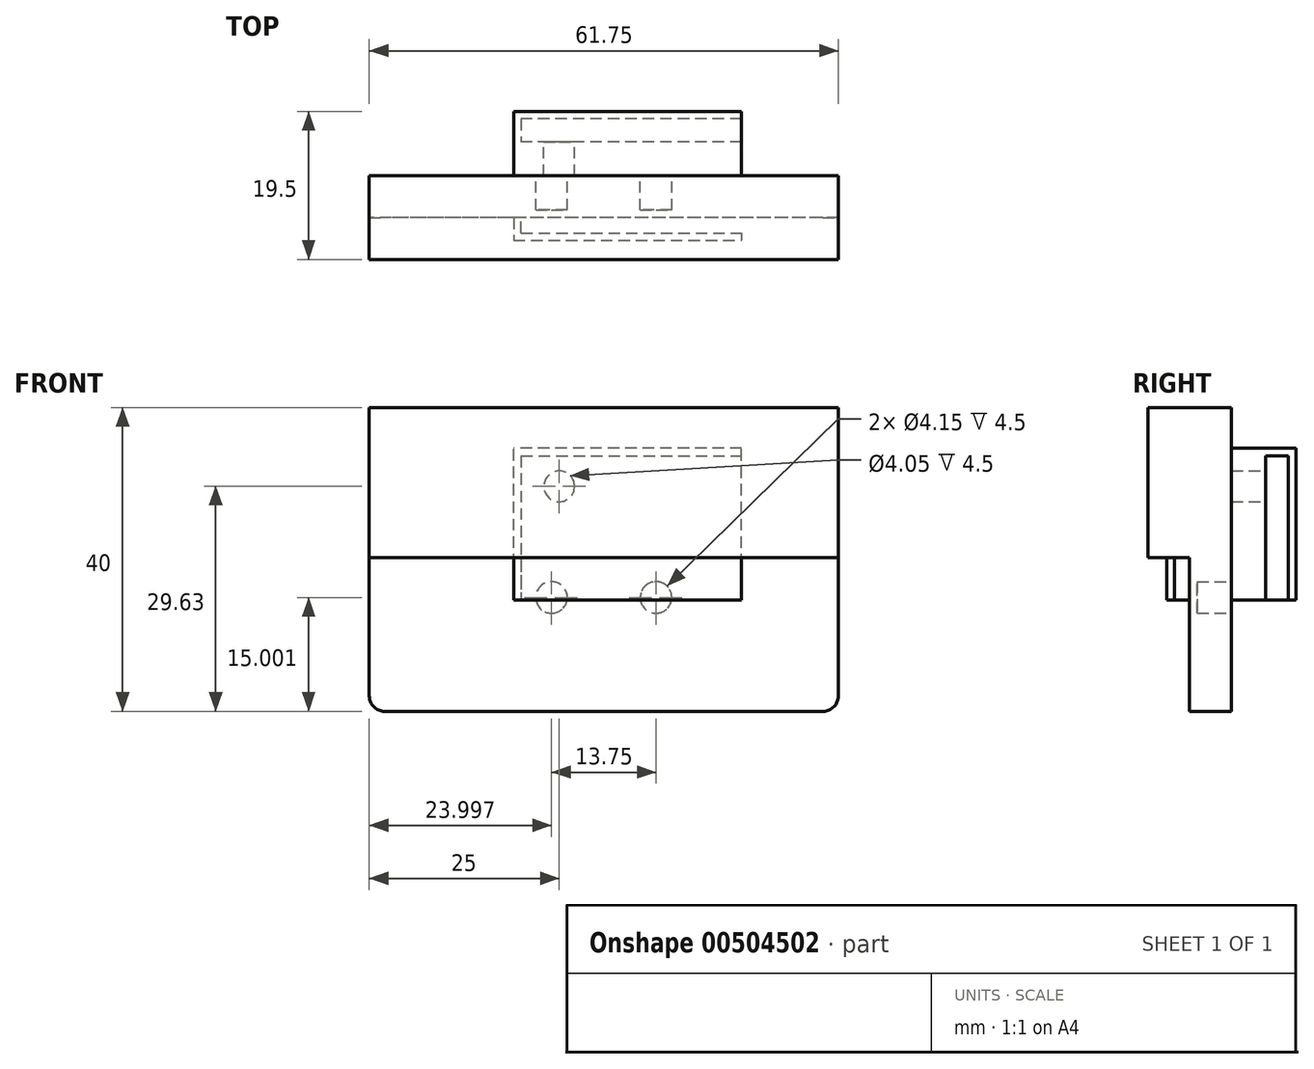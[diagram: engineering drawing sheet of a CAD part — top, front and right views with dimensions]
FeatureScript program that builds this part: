
annotation { "Feature Type Name" : "Feature", "Feature Type Description" : "" }
export const myFeature = defineFeature(function(context is Context, id is Id, definition is map)
    precondition{}
    {
        {
            var Q0;
            Q0=qCreatedBy(makeId("Front.planeOp"),FACE);
            var sketch = newSketch(context, id + "F0", { "sketchPlane" : qUnion([Q0])});
            skLineSegment(sketch, "E0.bottom", {"start": v(15, -10) * mm, "end": v(-15, -10) * mm});
            skLineSegment(sketch, "E0.top", {"start": v(15, 10) * mm, "end": v(-15, 10) * mm});
            skLineSegment(sketch, "E0.left", {"start": v(15, -10) * mm, "end": v(15, 10) * mm});
            skLineSegment(sketch, "E0.right", {"start": v(-15, -10) * mm, "end": v(-15, 10) * mm});
            skPoint(sketch, "E0.middle", {"position": v(0, 0) * mm});
            skPoint(sketch, "E1", {"position": v(-14, 9) * mm});
            skLineSegment(sketch, "E2", {"start": v(-14, 9) * mm, "end": v(15, 9) * mm});
            skLineSegment(sketch, "E3", {"start": v(-14, 9) * mm, "end": v(-14, -10) * mm});
            skCircle(sketch, "E4", {"center": v(-9, 5) * mm, "radius": 2.02 * mm});
            skSolve(sketch);
        }
        {
            var Q0;
            {var subQ1=sQuery(id+"F0.wireOp",EDGE,"E2");Q0=makeQuery(id+"F0.imprint","IMPRINT",FACE,{"disambiguationData":[TD([[makeQuery(id+"F0.imprint","IMPRINT",EDGE,{"derivedFrom":subQ1}),-1.0]])]});}
            var Q1;
            {var subQ2=sQuery(id+"F0.wireOp",EDGE,"E0.top");Q1=makeQuery(id+"F0.imprint","IMPRINT",FACE,{"disambiguationData":[TD([[makeQuery(id+"F0.imprint","IMPRINT",EDGE,{"derivedFrom":subQ2}),1.0]])]});}
            var Q2;
            Q2=makeQuery(id+"F0.imprint","IMPRINT",FACE,{"disambiguationData":[TD([[makeQuery(id+"F0.imprint","IMPRINT",EDGE,{"derivedFrom":sQuery(id+"F0.wireOp",EDGE,"E4")}),1.0]])]});
            extrude(context, id + "F1", {"entities" : qUnion([Q0, Q1, Q2]), "depth" : 8.5 * mm});
        }
        {
            var Q0;
            {var subQ1=sQuery(id+"F0.wireOp",EDGE,"E2");Q0=makeQuery(id+"F0.imprint","IMPRINT",FACE,{"disambiguationData":[TD([[makeQuery(id+"F0.imprint","IMPRINT",EDGE,{"derivedFrom":subQ1}),-1.0]])]});}
            var Q1;
            Q1=makeQuery(id+"F0.imprint","IMPRINT",FACE,{"disambiguationData":[TD([[makeQuery(id+"F0.imprint","IMPRINT",EDGE,{"derivedFrom":sQuery(id+"F0.wireOp",EDGE,"E4")}),1.0]])]});
            extrude(context, id + "F2", {"entities" : qUnion([Q0, Q1]), "operationType" : NewBodyOperationType.REMOVE, "depth" : 7.5 * mm});
        }
        {
            var Q0;
            {var subQ1=sQuery(id+"F0.wireOp",EDGE,"E2");Q0=makeQuery(id+"F0.imprint","IMPRINT",FACE,{"disambiguationData":[TD([[makeQuery(id+"F0.imprint","IMPRINT",EDGE,{"derivedFrom":subQ1}),-1.0]])]});}
            extrude(context, id + "F3", {"entities" : qUnion([Q0]), "operationType" : NewBodyOperationType.ADD, "depth" : 4.5 * mm});
        }
        {
            var Q0;
            {var subQ1=sQuery(id+"F0.wireOp",EDGE,"E2");Q0=makeQuery(id+"F0.imprint","IMPRINT",FACE,{"disambiguationData":[TD([[makeQuery(id+"F0.imprint","IMPRINT",EDGE,{"derivedFrom":subQ1}),-1.0]])]});}
            var Q1;
            Q1=makeQuery(id+"F0.imprint","IMPRINT",FACE,{"disambiguationData":[TD([[makeQuery(id+"F0.imprint","IMPRINT",EDGE,{"derivedFrom":sQuery(id+"F0.wireOp",EDGE,"E4")}),1.0]])]});
            var Q2;
            {var subQ2=sQuery(id+"F0.wireOp",EDGE,"E0.top");Q2=makeQuery(id+"F0.imprint","IMPRINT",FACE,{"disambiguationData":[TD([[makeQuery(id+"F0.imprint","IMPRINT",EDGE,{"derivedFrom":subQ2}),1.0]])]});}
            extrude(context, id + "F4", {"entities" : qUnion([Q0, Q1, Q2]), "oppositeDirection" : true, "depth" : 8.5 * mm});
        }
        {
            var Q0;
            {var subQ1=sQuery(id+"F0.wireOp",EDGE,"E2");Q0=makeQuery(id+"F0.imprint","IMPRINT",FACE,{"disambiguationData":[TD([[makeQuery(id+"F0.imprint","IMPRINT",EDGE,{"derivedFrom":subQ1}),-1.0]])]});}
            var Q1;
            Q1=makeQuery(id+"F0.imprint","IMPRINT",FACE,{"disambiguationData":[TD([[makeQuery(id+"F0.imprint","IMPRINT",EDGE,{"derivedFrom":sQuery(id+"F0.wireOp",EDGE,"E4")}),1.0]])]});
            extrude(context, id + "F5", {"entities" : qUnion([Q0, Q1]), "operationType" : NewBodyOperationType.REMOVE, "oppositeDirection" : true, "depth" : 7.5 * mm});
        }
        {
            var Q0;
            {var subQ1=sQuery(id+"F0.wireOp",EDGE,"E2");Q0=makeQuery(id+"F0.imprint","IMPRINT",FACE,{"disambiguationData":[TD([[makeQuery(id+"F0.imprint","IMPRINT",EDGE,{"derivedFrom":subQ1}),-1.0]])]});}
            extrude(context, id + "F6", {"entities" : qUnion([Q0]), "operationType" : NewBodyOperationType.ADD, "oppositeDirection" : true, "depth" : 4.5 * mm});
        }
        {
            var Q0;
            Q0=qCreatedBy(makeId("Front.planeOp"),FACE);
            var sketch = newSketch(context, id + "F7", { "sketchPlane" : qUnion([Q0])});
            skLineSegment(sketch, "E5.bottom", {"start": v(25.75, -24.63) * mm, "end": v(-32, -24.63) * mm});
            skLineSegment(sketch, "E5.top", {"start": v(27.75, 15.37) * mm, "end": v(-34, 15.37) * mm});
            skLineSegment(sketch, "E5.left", {"start": v(27.75, -22.63) * mm, "end": v(27.75, 15.37) * mm});
            skLineSegment(sketch, "E5.right", {"start": v(-34, -22.63) * mm, "end": v(-34, 15.37) * mm});
            skLineSegment(sketch, "E6", {"start": v(27.75, -4.38) * mm, "end": v(-34, -4.38) * mm});
            skPoint(sketch, "E7", {"position": v(3.75, -9.63) * mm});
            skPoint(sketch, "E8", {"position": v(-10, -9.63) * mm});
            skCircle(sketch, "E9", {"center": v(3.75, -9.63) * mm, "radius": 2.08 * mm});
            skCircle(sketch, "E10", {"center": v(-10, -9.63) * mm, "radius": 2.08 * mm});
            skPoint(sketch, "E11.visualSharp", {"position": v(27.75, -24.63) * mm});
            skArc(sketch, "E11.filletArc", {"start": v(25.75, -24.63) * mm, "mid": v(27.16, -24.04) * mm, "end": v(27.75, -22.63) * mm});
            skPoint(sketch, "E12.visualSharp", {"position": v(-34, -24.63) * mm});
            skArc(sketch, "E12.filletArc", {"start": v(-34, -22.63) * mm, "mid": v(-33.42, -24.04) * mm, "end": v(-32, -24.63) * mm});
            skSolve(sketch);
        }
        {
            var Q0;
            Q0=makeQuery(id+"F7.imprint","IMPRINT",FACE,{"disambiguationData":[TD([[makeQuery(id+"F7.imprint","IMPRINT",EDGE,{"derivedFrom":sQuery(id+"F7.wireOp",EDGE,"E9")}),1.0]])]});
            var Q1;
            Q1=makeQuery(id+"F7.imprint","IMPRINT",FACE,{"disambiguationData":[TD([[makeQuery(id+"F7.imprint","IMPRINT",EDGE,{"derivedFrom":sQuery(id+"F7.wireOp",EDGE,"E10")}),1.0]])]});
            var Q2;
            Q2=makeQuery(id+"F7.imprint","IMPRINT",FACE,{"disambiguationData":[TD([[makeQuery(id+"F7.imprint","IMPRINT",EDGE,{"derivedFrom":sQuery(id+"F7.wireOp",EDGE,"E5.bottom")}),-1.0]])]});
            extrude(context, id + "F8", {"entities" : qUnion([Q0, Q1, Q2]), "depth" : 5.5 * mm, "offsetDistance" : 25 * mm});
        }
        {
            var Q0;
            Q0=makeQuery(id+"F7.imprint","IMPRINT",FACE,{"disambiguationData":[TD([[makeQuery(id+"F7.imprint","IMPRINT",EDGE,{"derivedFrom":sQuery(id+"F7.wireOp",EDGE,"E10")}),1.0]])]});
            var Q1;
            Q1=makeQuery(id+"F7.imprint","IMPRINT",FACE,{"disambiguationData":[TD([[makeQuery(id+"F7.imprint","IMPRINT",EDGE,{"derivedFrom":sQuery(id+"F7.wireOp",EDGE,"E9")}),1.0]])]});
            extrude(context, id + "F9", {"entities" : qUnion([Q0, Q1]), "operationType" : NewBodyOperationType.REMOVE, "depth" : 4.5 * mm, "offsetDistance" : 25 * mm});
        }
        {
            var Q0;
            {var subQ0=sQuery(id+"F7.wireOp",EDGE,"E5.top");Q0=makeQuery(id+"F7.imprint","IMPRINT",FACE,{"disambiguationData":[TD([[makeQuery(id+"F7.imprint","IMPRINT",EDGE,{"derivedFrom":subQ0}),1.0]])]});}
            extrude(context, id + "F10", {"entities" : qUnion([Q0]), "operationType" : NewBodyOperationType.ADD, "depth" : 11 * mm, "offsetDistance" : 25 * mm});
        }
    });
